# Revit family: FU_Booth_Sandler_Cocoon-102
name_source: partatom
category: Furniture
units: mm (PartAtom-declared; Revit-internal decimal feet)

## family parameters
Always vertical = Yes
Cut with Voids When Loaded = No
OmniClass Number = 23.40.20.00
OmniClass Title = General Furniture and Specialties
Room Calculation Point = No
Shared = No
Work Plane-Based = No

## types (1)
- Cocoon 102
    Default Elevation = 0 mm  [stored 0 ft]
    Depth = 940 mm  [stored 3.08399 ft]
    Description = Acoustic seating unit which provides privacy and personal space. Fitted with built-in Bluetooth speakers (1-way Bluetooth), LED lighting, USB charger and mounted on casters. Rechargeable battery lasts for 2-3 daysdepending on usage.
    Height = 1760 mm  [stored 5.77428 ft]
    Manufacturer = Sandler
    Model = Cocoon 102
    URL = https://www.sandlerseating.com
    Width = 1000 mm  [stored 3.28084 ft]

note: [stored X ft] marks values corroborated as IEEE doubles in the binary element streams (Revit-internal decimal feet)

## geometry (parser evidence)
native form markers: Sweep x6
no freeform markers — native parametric forms only
